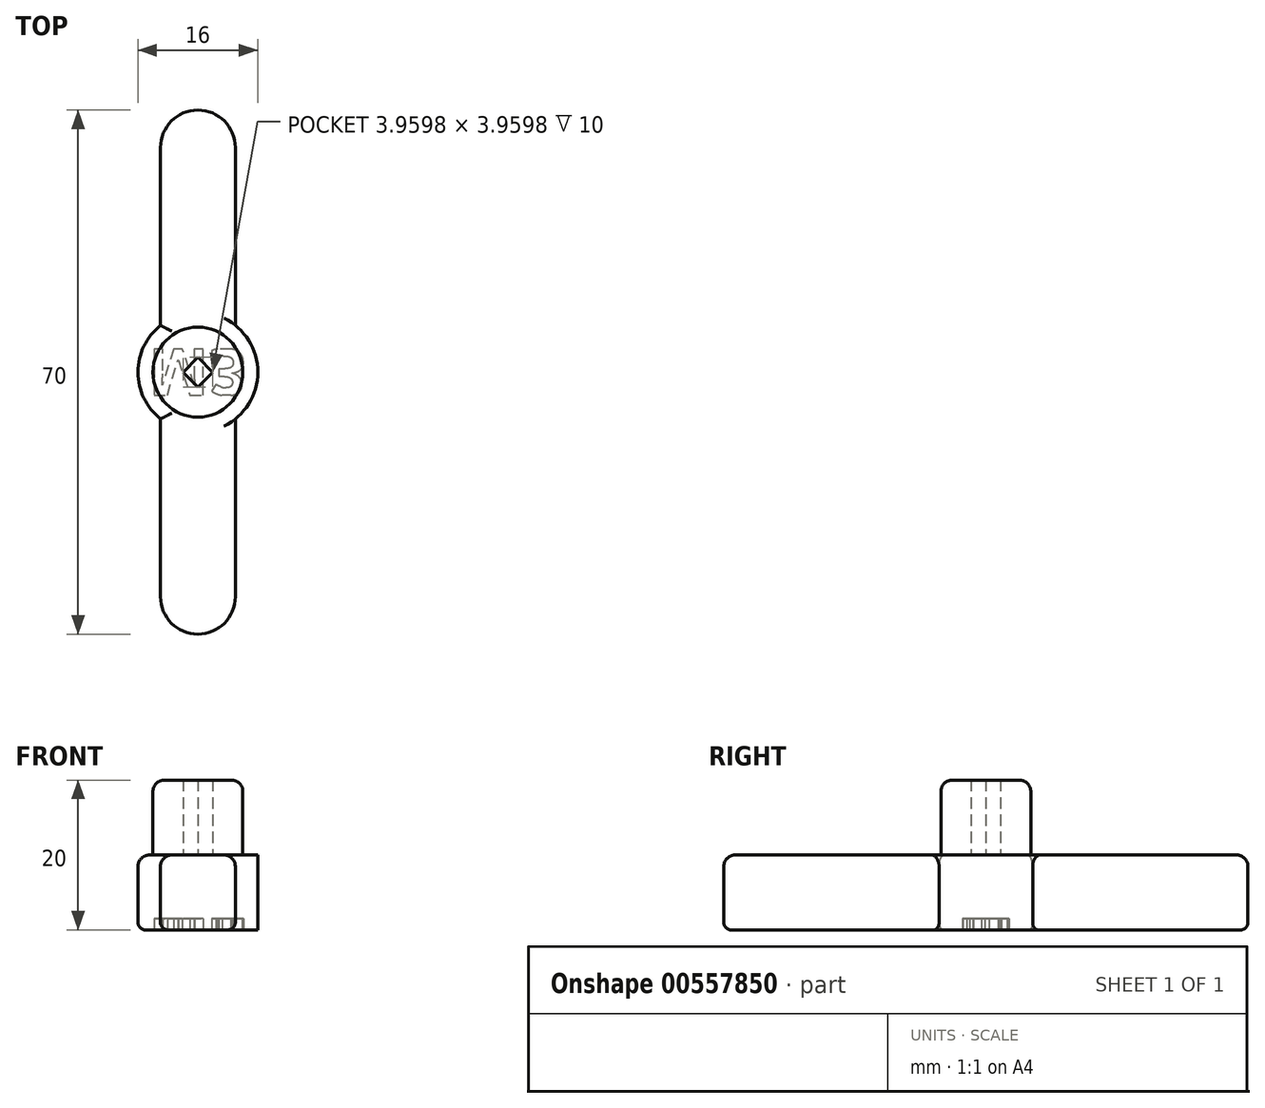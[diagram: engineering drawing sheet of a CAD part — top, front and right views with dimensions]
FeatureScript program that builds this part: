
annotation { "Feature Type Name" : "Feature", "Feature Type Description" : "" }
export const myFeature = defineFeature(function(context is Context, id is Id, definition is map)
    precondition{}
    {
        {
            var Q0;
            Q0=qCreatedBy(makeId("Top.planeOp"),FACE);
            var sketch = newSketch(context, id + "F0", { "sketchPlane" : qUnion([Q0])});
            skLineSegment(sketch, "E0.bottom", {"start": v(5, -30) * mm, "end": v(-5, -30) * mm});
            skLineSegment(sketch, "E0.top", {"start": v(5, 30) * mm, "end": v(-5, 30) * mm});
            skLineSegment(sketch, "E0.left", {"start": v(5, -30) * mm, "end": v(5, 30) * mm});
            skLineSegment(sketch, "E0.right", {"start": v(-5, -30) * mm, "end": v(-5, 30) * mm});
            skPoint(sketch, "E0.middle", {"position": v(0, 0) * mm});
            skArc(sketch, "E1", {"start": v(5, 30) * mm, "mid": v(0, 35) * mm, "end": v(-5, 30) * mm});
            skArc(sketch, "E2", {"start": v(-5, -30) * mm, "mid": v(0, -35) * mm, "end": v(5, -30) * mm});
            skCircle(sketch, "E3", {"center": v(0, 0) * mm, "radius": 8 * mm});
            skCircle(sketch, "E4", {"center": v(0, 0) * mm, "radius": 6 * mm});
            skCircle(sketch, "E5.cCircle", {"center": v(0, 0) * mm, "radius": 2.83 * mm, "construction": true});
            skLineSegment(sketch, "E5.0", {"start": v(0, -2.83) * mm, "end": v(-2.83, 0) * mm});
            skLineSegment(sketch, "E5.1", {"start": v(-2.83, 0) * mm, "end": v(0, 2.83) * mm});
            skLineSegment(sketch, "E5.2", {"start": v(0, 2.83) * mm, "end": v(2.83, 0) * mm});
            skLineSegment(sketch, "E5.3", {"start": v(2.83, 0) * mm, "end": v(0, -2.83) * mm});
            skSolve(sketch);
        }
        {
            var Q0;
            Q0=makeQuery(id+"F0.imprint","IMPRINT",FACE,{"disambiguationData":[TD([[makeQuery(id+"F0.imprint","IMPRINT",EDGE,{"derivedFrom":sQuery(id+"F0.wireOp",EDGE,"E5.0")}),1.0]])]});
            var Q1;
            {var subQ0=sQuery(id+"F0.wireOp",EDGE,"E4");var subQ1=sQuery(id+"F0.wireOp",EDGE,"E0.left");var subQ2=makeQuery(id+"F0.imprint","INTERSECT",VERTEX,{"disambiguationData":[OD(0.0)],"derivedFrom":[subQ1,subQ0]});Q1=makeQuery(id+"F0.imprint","IMPRINT",FACE,{"disambiguationData":[TD([[makeQuery(id+"F0.imprint","IMPRINT",EDGE,{"disambiguationData":[TD([[subQ2,-1.0]])],"derivedFrom":subQ1}),-1.0]])]});}
            var Q2;
            {var subQ0=sQuery(id+"F0.wireOp",EDGE,"E4");var subQ1=sQuery(id+"F0.wireOp",EDGE,"E0.right");var subQ2=makeQuery(id+"F0.imprint","INTERSECT",VERTEX,{"disambiguationData":[OD(0.0)],"derivedFrom":[subQ1,subQ0]});Q2=makeQuery(id+"F0.imprint","IMPRINT",FACE,{"disambiguationData":[TD([[makeQuery(id+"F0.imprint","IMPRINT",EDGE,{"disambiguationData":[TD([[subQ2,-1.0]])],"derivedFrom":subQ1}),1.0]])]});}
            extrude(context, id + "F1", {"entities" : qUnion([Q0, Q1, Q2]), "depth" : 20 * mm, "offsetDistance" : 25 * mm});
        }
        {
            var Q0;
            Q0=qSketchRegion(id+"F0",true);
            extrude(context, id + "F2", {"entities" : qUnion([Q0]), "operationType" : NewBodyOperationType.ADD, "depth" : 10 * mm, "offsetDistance" : 25 * mm});
        }
        {
            var Q0;
            Q0=qCreatedBy(makeId("Top.planeOp"),FACE);
            var sketch = newSketch(context, id + "F3", { "sketchPlane" : qUnion([Q0])});
            skCircle(sketch, "E6", {"center": v(0, 0) * mm, "radius": 3.52 * mm});
            skSolve(sketch);
        }
        {
            var Q0;
            Q0=makeQuery(id+"F3.imprint","IMPRINT",FACE,{"disambiguationData":[TD([[makeQuery(id+"F3.imprint","IMPRINT",EDGE,{"derivedFrom":sQuery(id+"F3.wireOp",EDGE,"E6")}),1.0]])]});
            extrude(context, id + "F4", {"entities" : qUnion([Q0]), "operationType" : NewBodyOperationType.ADD, "depth" : 10 * mm, "offsetDistance" : 25 * mm});
        }
        {
            var Q0;
            {var subQ0=sQuery(id+"F0.wireOp",EDGE,"E4");Q0=makeQuery(id+"F4.boolean.opBoolean","MERGE",FACE,{"derivedFrom":[makeQuery(id+"F2.boolean.opBoolean","MERGE",FACE,{"derivedFrom":[makeQuery(id+"F1.opExtrude","CAP_FACE",FACE,{"disambiguationData":[OSD([subQ0,sQuery(id+"F0.wireOp",EDGE,"E5.0"),sQuery(id+"F0.wireOp",EDGE,"E5.1"),sQuery(id+"F0.wireOp",EDGE,"E5.2"),sQuery(id+"F0.wireOp",EDGE,"E5.3")])],"isStart":true}),makeQuery(id+"F2.opExtrude","CAP_FACE",FACE,{"disambiguationData":[OSD([sQuery(id+"F0.wireOp",EDGE,"E0.left"),sQuery(id+"F0.wireOp",EDGE,"E0.right"),sQuery(id+"F0.wireOp",EDGE,"E1"),sQuery(id+"F0.wireOp",EDGE,"E2"),sQuery(id+"F0.wireOp",EDGE,"E3"),subQ0])],"isStart":true})]}),makeQuery(id+"F4.opExtrude","CAP_FACE",FACE,{"disambiguationData":[OSD([sQuery(id+"F3.wireOp",EDGE,"E6")])],"isStart":true})]});}
            var sketch = newSketch(context, id + "F5", { "sketchPlane" : qUnion([Q0])});
            skLineSegment(sketch, "E7.bottom", {"start": v(6.64, -3.1) * mm, "end": v(-6.64, -3.1) * mm});
            skLineSegment(sketch, "E7.top", {"start": v(6.64, 3.1) * mm, "end": v(-6.64, 3.1) * mm});
            skLineSegment(sketch, "E7.left", {"start": v(6.64, -3.1) * mm, "end": v(6.64, 3.1) * mm});
            skLineSegment(sketch, "E7.right", {"start": v(-6.64, -3.1) * mm, "end": v(-6.64, 3.1) * mm});
            skPoint(sketch, "E7.middle", {"position": v(0, 0) * mm});
            skText(sketch, "E8", { "text": "M3\n", "fontName": "OpenSans-Bold.ttf"});
            const initialGuessF5  = {"E8": [-0.00664, -0.0031, 1, 0, 0.00621]};
            skSetInitialGuess(sketch, initialGuessF5);
            skSolve(sketch);
        }
        {
            var Q0;
            Q0=makeQuery(id+"F5.imprint","IMPRINT",FACE,{"disambiguationData":[TD([[makeQuery(id+"F5.imprint","IMPRINT",EDGE,{"derivedFrom":sQuery(id+"F5.wireOp",EDGE,"E8.sketch_text.stroke-19")}),-1.0]])]});
            var Q1;
            Q1=makeQuery(id+"F5.imprint","IMPRINT",FACE,{"disambiguationData":[TD([[makeQuery(id+"F5.imprint","IMPRINT",EDGE,{"derivedFrom":sQuery(id+"F5.wireOp",EDGE,"E8.sketch_text.stroke-0")}),-1.0]])]});
            extrude(context, id + "F6", {"entities" : qUnion([Q0, Q1]), "operationType" : NewBodyOperationType.REMOVE, "oppositeDirection" : true, "depth" : 1.5 * mm, "offsetDistance" : 25 * mm});
        }
        {
            var Q0;
            Q0=makeQuery(id+"F1.opExtrude","CAP_EDGE",EDGE,{"disambiguationData":[OSD([sQuery(id+"F0.wireOp",EDGE,"E4")])],"isStart":false});
            fillet(context, id + "F7", {"entities" : qUnion([Q0]), "radius" : 1.5 * mm, "tangentPropagation" : true, "allowEdgeOverflow" : false});
        }
        {
            var Q0;
            Q0=makeQuery(id+"F2.opExtrude","CAP_EDGE",EDGE,{"disambiguationData":[OSD([sQuery(id+"F0.wireOp",EDGE,"E2")])],"isStart":false});
            var Q1;
            {var subQ0=sQuery(id+"F0.wireOp",EDGE,"E0.right");Q1=makeQuery(id+"F2.opExtrude","CAP_EDGE",EDGE,{"disambiguationData":[OSD([subQ0]),TDD([makeQuery(id+"F0.imprint","IMPRINT",EDGE,{"disambiguationData":[TD([[makeQuery(id+"F0.imprint","INTERSECT",VERTEX,{"disambiguationData":[OD(0.0)],"derivedFrom":[subQ0,sQuery(id+"F0.wireOp",EDGE,"E3")]}),1.0]])],"derivedFrom":subQ0})])],"isStart":false});}
            var Q2;
            {var subQ0=sQuery(id+"F0.wireOp",EDGE,"E3");var subQ1=sQuery(id+"F0.wireOp",EDGE,"E0.right");Q2=makeQuery(id+"F2.opExtrude","CAP_EDGE",EDGE,{"disambiguationData":[OSD([subQ0]),TDD([makeQuery(id+"F0.imprint","IMPRINT",EDGE,{"disambiguationData":[TD([[makeQuery(id+"F0.imprint","INTERSECT",VERTEX,{"disambiguationData":[OD(0.0)],"derivedFrom":[subQ1,subQ0]}),1.0]])],"derivedFrom":subQ0})])],"isStart":false});}
            var Q3;
            {var subQ0=sQuery(id+"F0.wireOp",EDGE,"E0.right");Q3=makeQuery(id+"F2.opExtrude","CAP_EDGE",EDGE,{"disambiguationData":[OSD([subQ0]),TDD([makeQuery(id+"F0.imprint","IMPRINT",EDGE,{"disambiguationData":[TD([[makeQuery(id+"F0.imprint","INTERSECT",VERTEX,{"disambiguationData":[OD(1.0)],"derivedFrom":[subQ0,sQuery(id+"F0.wireOp",EDGE,"E3")]}),-1.0]])],"derivedFrom":subQ0})])],"isStart":false});}
            var Q4;
            Q4=makeQuery(id+"F2.opExtrude","CAP_EDGE",EDGE,{"disambiguationData":[OSD([sQuery(id+"F0.wireOp",EDGE,"E1")])],"isStart":false});
            var Q5;
            {var subQ0=sQuery(id+"F0.wireOp",EDGE,"E0.left");Q5=makeQuery(id+"F2.opExtrude","CAP_EDGE",EDGE,{"disambiguationData":[OSD([subQ0]),TDD([makeQuery(id+"F0.imprint","IMPRINT",EDGE,{"disambiguationData":[TD([[makeQuery(id+"F0.imprint","INTERSECT",VERTEX,{"disambiguationData":[OD(1.0)],"derivedFrom":[subQ0,sQuery(id+"F0.wireOp",EDGE,"E3")]}),-1.0]])],"derivedFrom":subQ0})])],"isStart":false});}
            var Q6;
            {var subQ0=sQuery(id+"F0.wireOp",EDGE,"E3");var subQ1=sQuery(id+"F0.wireOp",EDGE,"E0.left");Q6=makeQuery(id+"F2.opExtrude","CAP_EDGE",EDGE,{"disambiguationData":[OSD([subQ0]),TDD([makeQuery(id+"F0.imprint","IMPRINT",EDGE,{"disambiguationData":[TD([[makeQuery(id+"F0.imprint","INTERSECT",VERTEX,{"disambiguationData":[OD(0.0)],"derivedFrom":[subQ1,subQ0]}),-1.0]])],"derivedFrom":subQ0})])],"isStart":false});}
            var Q7;
            {var subQ0=sQuery(id+"F0.wireOp",EDGE,"E0.left");Q7=makeQuery(id+"F2.opExtrude","CAP_EDGE",EDGE,{"disambiguationData":[OSD([subQ0]),TDD([makeQuery(id+"F0.imprint","IMPRINT",EDGE,{"disambiguationData":[TD([[makeQuery(id+"F0.imprint","INTERSECT",VERTEX,{"disambiguationData":[OD(0.0)],"derivedFrom":[subQ0,sQuery(id+"F0.wireOp",EDGE,"E3")]}),1.0]])],"derivedFrom":subQ0})])],"isStart":false});}
            fillet(context, id + "F8", {"entities" : qUnion([Q0, Q1, Q2, Q3, Q4, Q5, Q6, Q7]), "radius" : 1.5 * mm, "tangentPropagation" : true, "allowEdgeOverflow" : false});
        }
        {
            var Q0;
            {var subQ0=sQuery(id+"F0.wireOp",EDGE,"E0.left");Q0=makeQuery(id+"F2.opExtrude","CAP_EDGE",EDGE,{"disambiguationData":[OSD([subQ0]),TDD([makeQuery(id+"F0.imprint","IMPRINT",EDGE,{"disambiguationData":[TD([[makeQuery(id+"F0.imprint","INTERSECT",VERTEX,{"disambiguationData":[OD(0.0)],"derivedFrom":[subQ0,sQuery(id+"F0.wireOp",EDGE,"E3")]}),1.0]])],"derivedFrom":subQ0})])],"isStart":true});}
            var Q1;
            Q1=makeQuery(id+"F2.opExtrude","CAP_EDGE",EDGE,{"disambiguationData":[OSD([sQuery(id+"F0.wireOp",EDGE,"E2")])],"isStart":true});
            var Q2;
            {var subQ0=sQuery(id+"F0.wireOp",EDGE,"E3");var subQ1=sQuery(id+"F0.wireOp",EDGE,"E0.right");Q2=makeQuery(id+"F2.opExtrude","CAP_EDGE",EDGE,{"disambiguationData":[OSD([subQ0]),TDD([makeQuery(id+"F0.imprint","IMPRINT",EDGE,{"disambiguationData":[TD([[makeQuery(id+"F0.imprint","INTERSECT",VERTEX,{"disambiguationData":[OD(0.0)],"derivedFrom":[subQ1,subQ0]}),1.0]])],"derivedFrom":subQ0})])],"isStart":true});}
            var Q3;
            {var subQ0=sQuery(id+"F0.wireOp",EDGE,"E0.right");Q3=makeQuery(id+"F2.opExtrude","CAP_EDGE",EDGE,{"disambiguationData":[OSD([subQ0]),TDD([makeQuery(id+"F0.imprint","IMPRINT",EDGE,{"disambiguationData":[TD([[makeQuery(id+"F0.imprint","INTERSECT",VERTEX,{"disambiguationData":[OD(0.0)],"derivedFrom":[subQ0,sQuery(id+"F0.wireOp",EDGE,"E3")]}),1.0]])],"derivedFrom":subQ0})])],"isStart":true});}
            var Q4;
            {var subQ0=sQuery(id+"F0.wireOp",EDGE,"E0.left");Q4=makeQuery(id+"F2.opExtrude","CAP_EDGE",EDGE,{"disambiguationData":[OSD([subQ0]),TDD([makeQuery(id+"F0.imprint","IMPRINT",EDGE,{"disambiguationData":[TD([[makeQuery(id+"F0.imprint","INTERSECT",VERTEX,{"disambiguationData":[OD(1.0)],"derivedFrom":[subQ0,sQuery(id+"F0.wireOp",EDGE,"E3")]}),-1.0]])],"derivedFrom":subQ0})])],"isStart":true});}
            var Q5;
            {var subQ0=sQuery(id+"F0.wireOp",EDGE,"E0.right");Q5=makeQuery(id+"F2.opExtrude","CAP_EDGE",EDGE,{"disambiguationData":[OSD([subQ0]),TDD([makeQuery(id+"F0.imprint","IMPRINT",EDGE,{"disambiguationData":[TD([[makeQuery(id+"F0.imprint","INTERSECT",VERTEX,{"disambiguationData":[OD(1.0)],"derivedFrom":[subQ0,sQuery(id+"F0.wireOp",EDGE,"E3")]}),-1.0]])],"derivedFrom":subQ0})])],"isStart":true});}
            var Q6;
            Q6=makeQuery(id+"F2.opExtrude","CAP_EDGE",EDGE,{"disambiguationData":[OSD([sQuery(id+"F0.wireOp",EDGE,"E1")])],"isStart":true});
            var Q7;
            {var subQ0=sQuery(id+"F0.wireOp",EDGE,"E3");var subQ1=sQuery(id+"F0.wireOp",EDGE,"E0.left");Q7=makeQuery(id+"F2.opExtrude","CAP_EDGE",EDGE,{"disambiguationData":[OSD([subQ0]),TDD([makeQuery(id+"F0.imprint","IMPRINT",EDGE,{"disambiguationData":[TD([[makeQuery(id+"F0.imprint","INTERSECT",VERTEX,{"disambiguationData":[OD(0.0)],"derivedFrom":[subQ1,subQ0]}),-1.0]])],"derivedFrom":subQ0})])],"isStart":true});}
            fillet(context, id + "F9", {"entities" : qUnion([Q0, Q1, Q2, Q3, Q4, Q5, Q6, Q7]), "radius" : 1 * mm, "tangentPropagation" : true, "allowEdgeOverflow" : false});
        }
        {
            var Q0;
            Q0=makeQuery(id+"F4.opExtrude","CAP_FACE",FACE,{"disambiguationData":[OSD([sQuery(id+"F3.wireOp",EDGE,"E6")])],"isStart":false});
            var sketch = newSketch(context, id + "F10", { "sketchPlane" : qUnion([Q0])});
            skCircle(sketch, "E9.cCircle", {"center": v(0, 0) * mm, "radius": 1.98 * mm, "construction": true});
            skLineSegment(sketch, "E9.0", {"start": v(0, 1.98) * mm, "end": v(1.98, 0) * mm});
            skLineSegment(sketch, "E9.1", {"start": v(1.98, 0) * mm, "end": v(0, -1.98) * mm});
            skLineSegment(sketch, "E9.2", {"start": v(0, -1.98) * mm, "end": v(-1.98, 0) * mm});
            skLineSegment(sketch, "E9.3", {"start": v(-1.98, 0) * mm, "end": v(0, 1.98) * mm});
            skSolve(sketch);
        }
        {
            var Q0;
            Q0=makeQuery(id+"F10.imprint","IMPRINT",FACE,{"disambiguationData":[TD([[makeQuery(id+"F10.imprint","IMPRINT",EDGE,{"derivedFrom":sQuery(id+"F10.wireOp",EDGE,"E9.0")}),1.0]])]});
            extrude(context, id + "F11", {"entities" : qUnion([Q0]), "operationType" : NewBodyOperationType.ADD, "depth" : 10 * mm, "offsetDistance" : 25 * mm});
        }
    });
